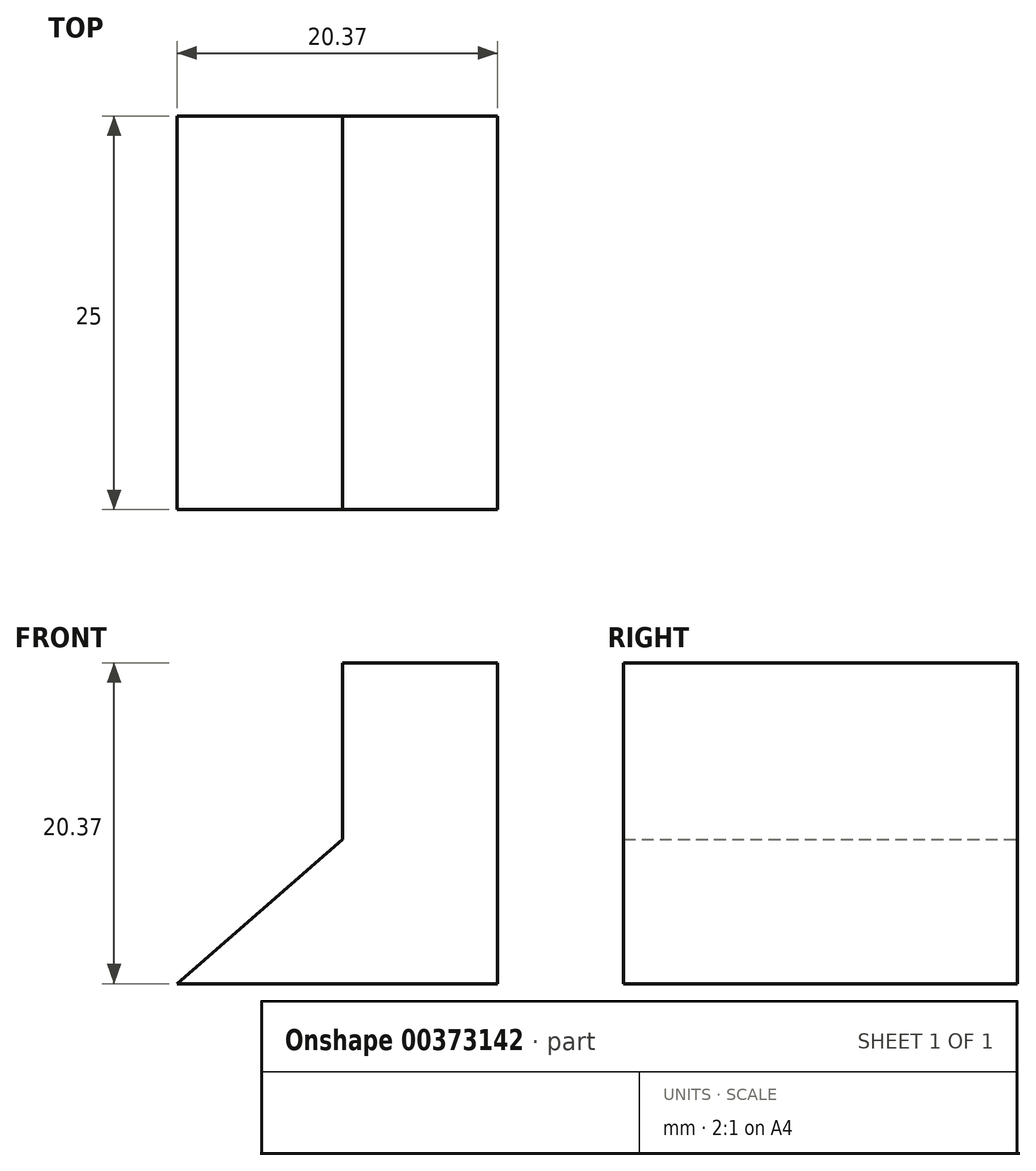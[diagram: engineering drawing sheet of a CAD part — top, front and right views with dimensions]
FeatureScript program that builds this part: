
annotation { "Feature Type Name" : "Feature", "Feature Type Description" : "" }
export const myFeature = defineFeature(function(context is Context, id is Id, definition is map)
    precondition{}
    {
        {
            var Q0;
            Q0=qCreatedBy(makeId("Front.planeOp"),FACE);
            var sketch = newSketch(context, id + "F0", { "sketchPlane" : qUnion([Q0])});
            skLineSegment(sketch, "E0", {"start": v(0, 0) * mm, "end": v(0, 20.37) * mm});
            skLineSegment(sketch, "E1", {"start": v(0, 0) * mm, "end": v(-20.37, 0) * mm});
            skLineSegment(sketch, "E2", {"start": v(-20.37, 0) * mm, "end": v(-9.84, 9.16) * mm});
            skLineSegment(sketch, "E3", {"start": v(0, 20.37) * mm, "end": v(-9.84, 20.37) * mm});
            skLineSegment(sketch, "E4", {"start": v(-9.84, 9.16) * mm, "end": v(-9.84, 20.37) * mm});
            skSolve(sketch);
        }
        {
            var Q0;
            Q0 = qSketchRegion(id + "F0", true);
            extrude(context, id + "F1", {"entities" : qUnion([Q0]), "depth" : 25 * mm});
        }
    });
